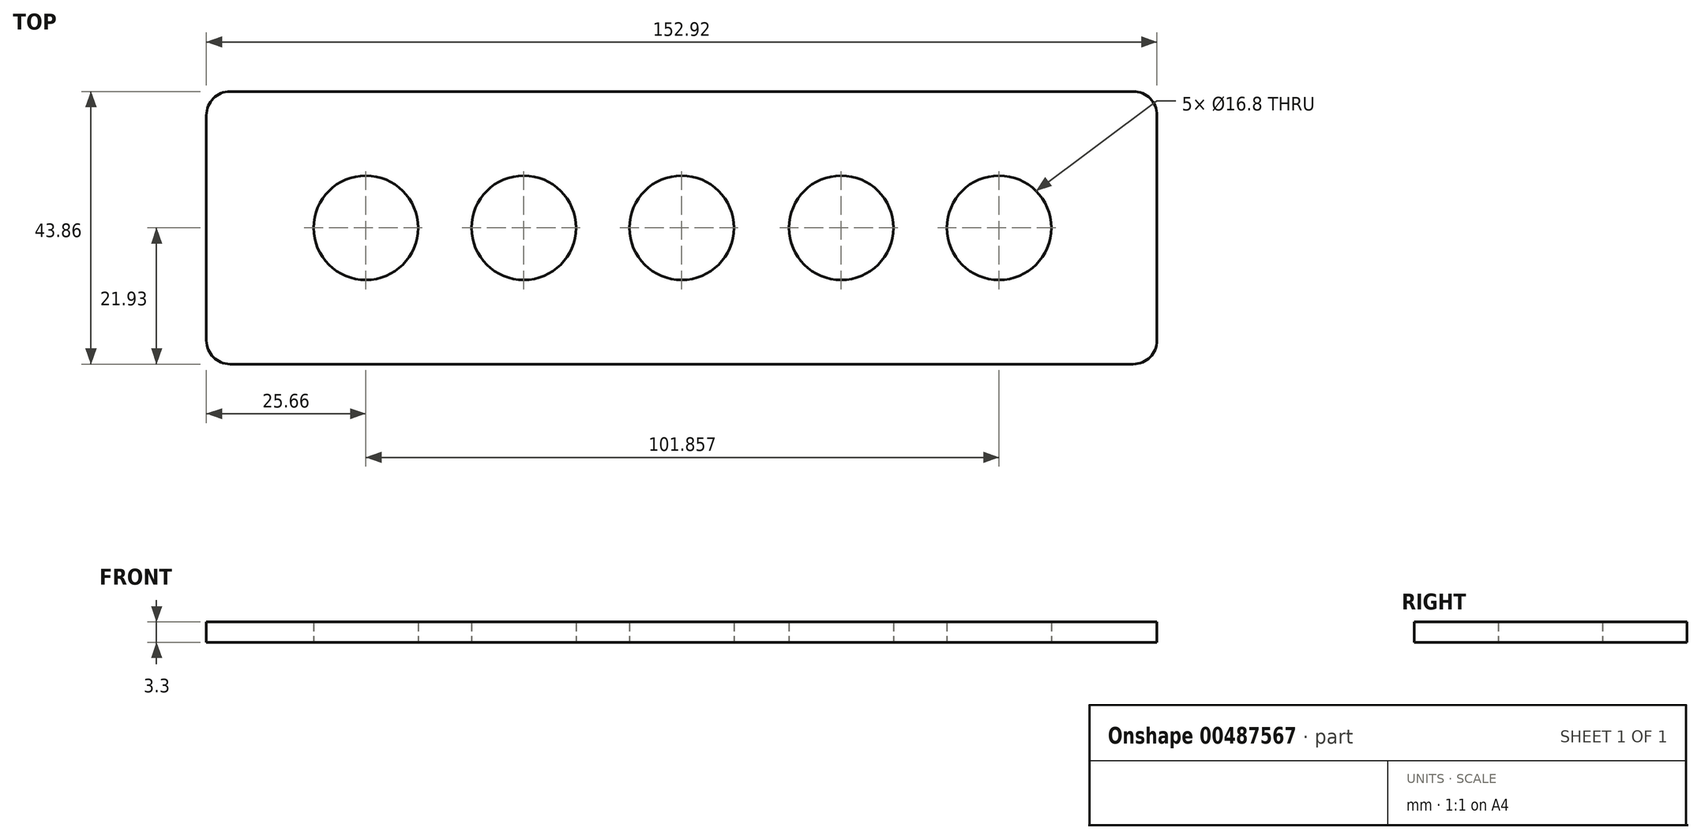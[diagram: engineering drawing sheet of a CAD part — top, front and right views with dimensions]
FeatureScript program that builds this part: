
annotation { "Feature Type Name" : "Feature", "Feature Type Description" : "" }
export const myFeature = defineFeature(function(context is Context, id is Id, definition is map)
    precondition{}
    {
        {
            var Q0;
            Q0=qCreatedBy(makeId("Top.planeOp"),FACE);
            var sketch = newSketch(context, id + "F0", { "sketchPlane" : qUnion([Q0])});
            skLineSegment(sketch, "E0.bottom", {"start": v(72.65, -21.93) * mm, "end": v(-72.65, -21.93) * mm});
            skLineSegment(sketch, "E0.top", {"start": v(72.65, 21.93) * mm, "end": v(-72.65, 21.93) * mm});
            skLineSegment(sketch, "E0.left", {"start": v(76.46, -18.12) * mm, "end": v(76.46, 18.12) * mm});
            skLineSegment(sketch, "E0.right", {"start": v(-76.46, -18.12) * mm, "end": v(-76.46, 18.12) * mm});
            skPoint(sketch, "E0.middle", {"position": v(0, 0) * mm});
            skPoint(sketch, "E1.visualSharp", {"position": v(-76.46, 21.93) * mm});
            skArc(sketch, "E1.filletArc", {"start": v(-72.65, 21.93) * mm, "mid": v(-75.34, 20.82) * mm, "end": v(-76.46, 18.12) * mm});
            skPoint(sketch, "E2.visualSharp", {"position": v(76.46, 21.93) * mm});
            skArc(sketch, "E2.filletArc", {"start": v(76.46, 18.12) * mm, "mid": v(75.34, 20.82) * mm, "end": v(72.65, 21.93) * mm});
            skPoint(sketch, "E3.visualSharp", {"position": v(76.46, -21.93) * mm});
            skArc(sketch, "E3.filletArc", {"start": v(72.65, -21.93) * mm, "mid": v(75.34, -20.82) * mm, "end": v(76.46, -18.12) * mm});
            skPoint(sketch, "E4.visualSharp", {"position": v(-76.46, -21.93) * mm});
            skArc(sketch, "E4.filletArc", {"start": v(-76.46, -18.12) * mm, "mid": v(-75.34, -20.82) * mm, "end": v(-72.65, -21.93) * mm});
            skCircle(sketch, "E5", {"center": v(-50.8, 0) * mm, "radius": 8.4 * mm});
            skCircle(sketch, "E6", {"center": v(-25.4, 0) * mm, "radius": 8.4 * mm});
            skCircle(sketch, "E7", {"center": v(25.66, 0) * mm, "radius": 8.4 * mm});
            skCircle(sketch, "E8", {"center": v(51.06, 0) * mm, "radius": 8.4 * mm});
            skCircle(sketch, "E9", {"center": v(0, 0) * mm, "radius": 8.4 * mm});
            skSolve(sketch);
        }
        {
            var Q0;
            Q0 = qSketchRegion(id + "F0", true);
            extrude(context, id + "F1", {"entities" : qUnion([Q0]), "depth" : 3.3 * mm, "offsetDistance" : 25.4 * mm});
        }
    });
